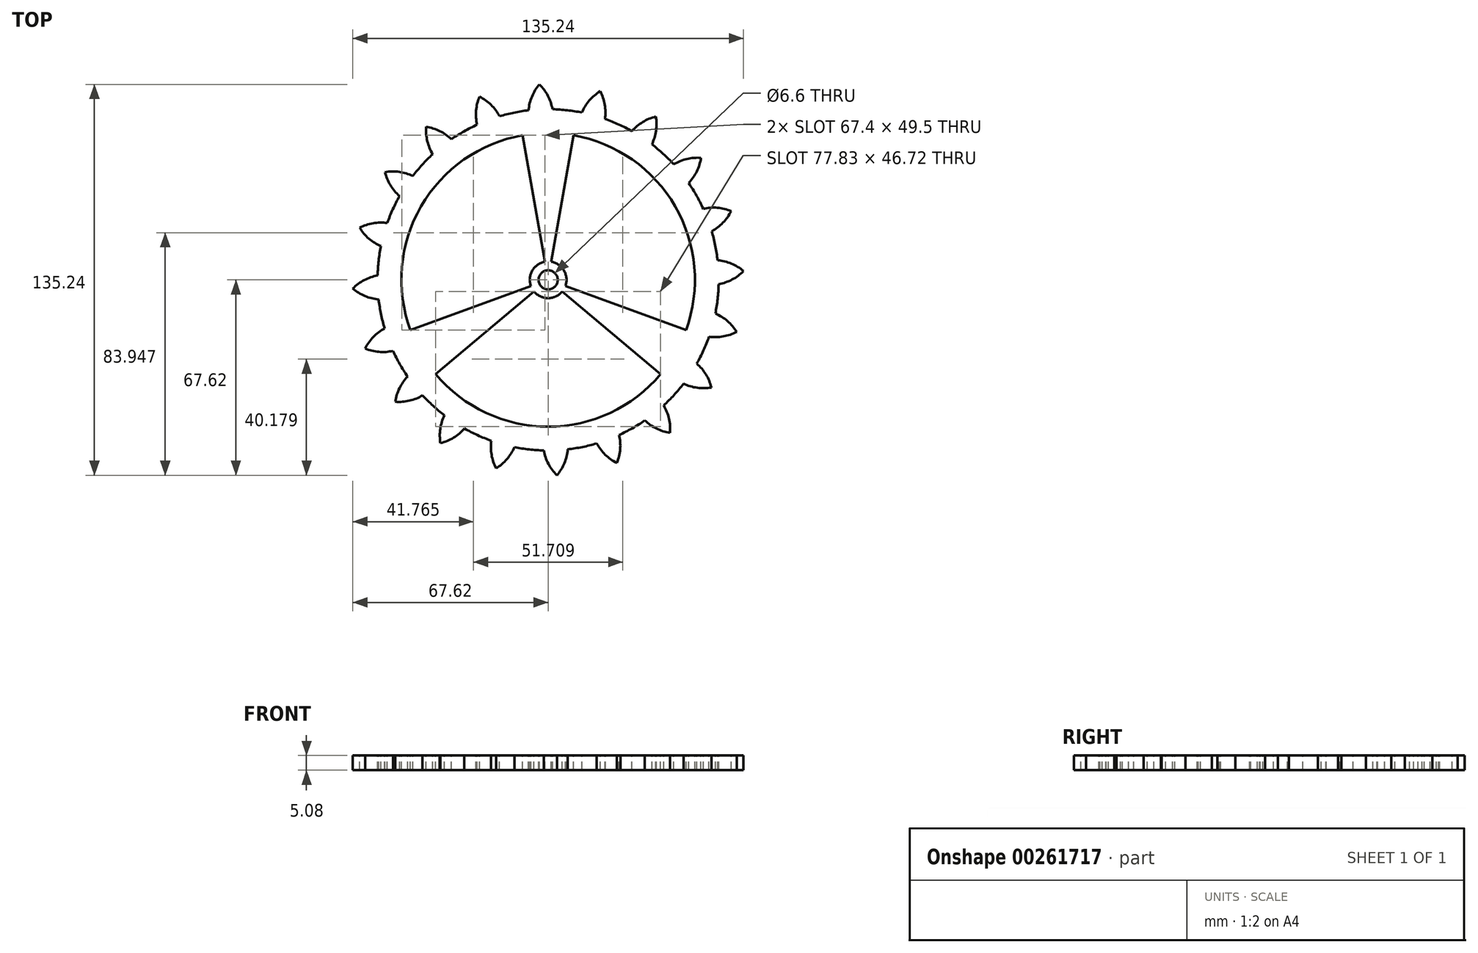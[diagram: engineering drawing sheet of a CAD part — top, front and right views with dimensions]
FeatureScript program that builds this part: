
annotation { "Feature Type Name" : "Feature", "Feature Type Description" : "" }
export const myFeature = defineFeature(function(context is Context, id is Id, definition is map)
    precondition{}
    {
        {
            var Q0;
            Q0=qCreatedBy(makeId("Top.planeOp"),FACE);
            var sketch = newSketch(context, id + "F0", { "sketchPlane" : qUnion([Q0])});
            skCircle(sketch, "E0", {"center": v(0, 0) * mm, "radius": 59.06 * mm});
            skSolve(sketch);
        }
        {
            var Q0;
            Q0=qSketchRegion(id+"F0",true);
            extrude(context, id + "F1", {"entities" : qUnion([Q0]), "depth" : 5.08 * mm});
        }
        {
            var Q0;
            Q0=makeQuery(id+"F1.opExtrude","CAP_FACE",FACE,{"disambiguationData":[OSD([sQuery(id+"F0.wireOp",EDGE,"E0")])],"isStart":false});
            var sketch = newSketch(context, id + "F2", { "sketchPlane" : qUnion([Q0])});
            skCircle(sketch, "E1", {"center": v(0, 0) * mm, "radius": 67.13 * mm, "construction": true});
            skCircle(sketch, "E2", {"center": v(0, 0) * mm, "radius": 63.5 * mm, "construction": true});
            skCircle(sketch, "E3", {"center": v(0, 0) * mm, "radius": 58.96 * mm, "construction": true});
            skLineSegment(sketch, "E4", {"start": v(0, 0) * mm, "end": v(0, 86.86) * mm, "construction": true});
            skLineSegment(sketch, "E5", {"start": v(0, 0) * mm, "end": v(-3.86, 85.95) * mm, "construction": true});
            skLineSegment(sketch, "E6", {"start": v(0, 63.5) * mm, "end": v(-65.71, 63.5) * mm, "construction": true});
            skLineSegment(sketch, "E7", {"start": v(0, 63.5) * mm, "end": v(-58.85, 37.3) * mm, "construction": true});
            skCircle(sketch, "E8", {"center": v(0, 63.5) * mm, "radius": 15.88 * mm, "construction": true});
            skCircle(sketch, "E9", {"center": v(0, 0) * mm, "radius": 58.01 * mm, "construction": true});
            skCircle(sketch, "E10", {"center": v(-14.13, 56.26) * mm, "radius": 15.88 * mm, "construction": true});
            skArc(sketch, "E11", {"start": v(1.52, 58.94) * mm, "mid": v(-0.07, 63.64) * mm, "end": v(-3.04, 67.62) * mm});
            skArc(sketch, "E12.MirrorCS", {"start": v(-6.8, 58.57) * mm, "mid": v(-5.63, 63.4) * mm, "end": v(-3.04, 67.62) * mm});
            skLineSegment(sketch, "E13", {"start": v(-6.8, 58.57) * mm, "end": v(1.52, 58.94) * mm});
            skPoint(sketch, "E14.orphan", {"position": v(-3.5, 67.04) * mm});
            skPoint(sketch, "E15.orphan", {"position": v(-2.51, 67.08) * mm});
            skSolve(sketch);
        }
        {
            var Q0;
            Q0=qSketchRegion(id+"F2",true);
            var Q1;
            Q1=makeQuery(id+"F1.opExtrude","CAP_FACE",FACE,{"disambiguationData":[OSD([sQuery(id+"F0.wireOp",EDGE,"E0")])],"isStart":true});
            extrude(context, id + "F3", {"entities" : qUnion([Q0]), "endBound" : BoundingType.UP_TO_SURFACE, "oppositeDirection" : true, "endBoundEntityFace" : qUnion([Q1]), "depth" : 25.4 * mm});
        }
        {
            var Q0;
            Q0=makeQuery(id+"F3.opExtrude","SWEPT_BODY",BODY,{"disambiguationData":[OSD([sQuery(id+"F2.wireOp",EDGE,"E11"),sQuery(id+"F2.wireOp",EDGE,"E12.MirrorCS"),sQuery(id+"F2.wireOp",EDGE,"E13")])]});
            var Q1;
            Q1=makeQuery(id+"F1.opExtrude","CAP_EDGE",EDGE,{"disambiguationData":[OSD([sQuery(id+"F0.wireOp",EDGE,"E0")])],"isStart":false});
            circularPattern(context, id + "F4", {"operationType" : NewBodyOperationType.ADD, "entities" : qUnion([Q0]), "axis" : qUnion([Q1]), "angle" : 360 * degree, "instanceCount" : 20, "equalSpace" : true});
        }
        {
            var Q0;
            {var subQ0=makeQuery(id+"F3.opExtrude","CAP_FACE",FACE,{"disambiguationData":[OSD([sQuery(id+"F2.wireOp",EDGE,"E11"),sQuery(id+"F2.wireOp",EDGE,"E12.MirrorCS"),sQuery(id+"F2.wireOp",EDGE,"E13")])],"isStart":true});Q0=makeQuery(id+"F4.boolean.opBoolean","MERGE",FACE,{"derivedFrom":[makeQuery(id+"F1.opExtrude","CAP_FACE",FACE,{"disambiguationData":[OSD([sQuery(id+"F0.wireOp",EDGE,"E0")])],"isStart":false}),subQ0,makeQuery(id+"F4.opPattern","COPY",FACE,{"derivedFrom":subQ0,"instanceName":"1"}),makeQuery(id+"F4.opPattern","COPY",FACE,{"derivedFrom":subQ0,"instanceName":"2"}),makeQuery(id+"F4.opPattern","COPY",FACE,{"derivedFrom":subQ0,"instanceName":"3"}),makeQuery(id+"F4.opPattern","COPY",FACE,{"derivedFrom":subQ0,"instanceName":"4"}),makeQuery(id+"F4.opPattern","COPY",FACE,{"derivedFrom":subQ0,"instanceName":"5"}),makeQuery(id+"F4.opPattern","COPY",FACE,{"derivedFrom":subQ0,"instanceName":"6"}),makeQuery(id+"F4.opPattern","COPY",FACE,{"derivedFrom":subQ0,"instanceName":"7"}),makeQuery(id+"F4.opPattern","COPY",FACE,{"derivedFrom":subQ0,"instanceName":"8"}),makeQuery(id+"F4.opPattern","COPY",FACE,{"derivedFrom":subQ0,"instanceName":"9"}),makeQuery(id+"F4.opPattern","COPY",FACE,{"derivedFrom":subQ0,"instanceName":"10"}),makeQuery(id+"F4.opPattern","COPY",FACE,{"derivedFrom":subQ0,"instanceName":"11"}),makeQuery(id+"F4.opPattern","COPY",FACE,{"derivedFrom":subQ0,"instanceName":"12"}),makeQuery(id+"F4.opPattern","COPY",FACE,{"derivedFrom":subQ0,"instanceName":"13"}),makeQuery(id+"F4.opPattern","COPY",FACE,{"derivedFrom":subQ0,"instanceName":"14"}),makeQuery(id+"F4.opPattern","COPY",FACE,{"derivedFrom":subQ0,"instanceName":"15"}),makeQuery(id+"F4.opPattern","COPY",FACE,{"derivedFrom":subQ0,"instanceName":"16"}),makeQuery(id+"F4.opPattern","COPY",FACE,{"derivedFrom":subQ0,"instanceName":"17"}),makeQuery(id+"F4.opPattern","COPY",FACE,{"derivedFrom":subQ0,"instanceName":"18"}),makeQuery(id+"F4.opPattern","COPY",FACE,{"derivedFrom":subQ0,"instanceName":"19"})]});}
            var sketch = newSketch(context, id + "F5", { "sketchPlane" : qUnion([Q0])});
            skCircle(sketch, "E16", {"center": v(0, 0) * mm, "radius": 50.8 * mm});
            skSolve(sketch);
        }
        {
            var Q0;
            Q0=qSketchRegion(id+"F5",true);
            extrude(context, id + "F6", {"entities" : qUnion([Q0]), "operationType" : NewBodyOperationType.REMOVE, "endBound" : BoundingType.THROUGH_ALL, "oppositeDirection" : true, "depth" : 25.4 * mm});
        }
        {
            var Q0;
            Q0=qSketchRegion(id+"F5",true);
            extrude(context, id + "F7", {"entities" : qUnion([Q0]), "operationType" : NewBodyOperationType.REMOVE, "endBound" : BoundingType.THROUGH_ALL, "oppositeDirection" : true, "depth" : 25.4 * mm});
        }
        {
            var Q0;
            {var subQ0=makeQuery(id+"F3.opExtrude","CAP_FACE",FACE,{"disambiguationData":[OSD([sQuery(id+"F2.wireOp",EDGE,"E11"),sQuery(id+"F2.wireOp",EDGE,"E12.MirrorCS"),sQuery(id+"F2.wireOp",EDGE,"E13")])],"isStart":true});Q0=makeQuery(id+"F4.boolean.opBoolean","MERGE",FACE,{"derivedFrom":[makeQuery(id+"F1.opExtrude","CAP_FACE",FACE,{"disambiguationData":[OSD([sQuery(id+"F0.wireOp",EDGE,"E0")])],"isStart":false}),subQ0,makeQuery(id+"F4.opPattern","COPY",FACE,{"derivedFrom":subQ0,"instanceName":"1"}),makeQuery(id+"F4.opPattern","COPY",FACE,{"derivedFrom":subQ0,"instanceName":"2"}),makeQuery(id+"F4.opPattern","COPY",FACE,{"derivedFrom":subQ0,"instanceName":"3"}),makeQuery(id+"F4.opPattern","COPY",FACE,{"derivedFrom":subQ0,"instanceName":"4"}),makeQuery(id+"F4.opPattern","COPY",FACE,{"derivedFrom":subQ0,"instanceName":"5"}),makeQuery(id+"F4.opPattern","COPY",FACE,{"derivedFrom":subQ0,"instanceName":"6"}),makeQuery(id+"F4.opPattern","COPY",FACE,{"derivedFrom":subQ0,"instanceName":"7"}),makeQuery(id+"F4.opPattern","COPY",FACE,{"derivedFrom":subQ0,"instanceName":"8"}),makeQuery(id+"F4.opPattern","COPY",FACE,{"derivedFrom":subQ0,"instanceName":"9"}),makeQuery(id+"F4.opPattern","COPY",FACE,{"derivedFrom":subQ0,"instanceName":"10"}),makeQuery(id+"F4.opPattern","COPY",FACE,{"derivedFrom":subQ0,"instanceName":"11"}),makeQuery(id+"F4.opPattern","COPY",FACE,{"derivedFrom":subQ0,"instanceName":"12"}),makeQuery(id+"F4.opPattern","COPY",FACE,{"derivedFrom":subQ0,"instanceName":"13"}),makeQuery(id+"F4.opPattern","COPY",FACE,{"derivedFrom":subQ0,"instanceName":"14"}),makeQuery(id+"F4.opPattern","COPY",FACE,{"derivedFrom":subQ0,"instanceName":"15"}),makeQuery(id+"F4.opPattern","COPY",FACE,{"derivedFrom":subQ0,"instanceName":"16"}),makeQuery(id+"F4.opPattern","COPY",FACE,{"derivedFrom":subQ0,"instanceName":"17"}),makeQuery(id+"F4.opPattern","COPY",FACE,{"derivedFrom":subQ0,"instanceName":"18"}),makeQuery(id+"F4.opPattern","COPY",FACE,{"derivedFrom":subQ0,"instanceName":"19"})]});}
            var sketch = newSketch(context, id + "F8", { "sketchPlane" : qUnion([Q0])});
            skArc(sketch, "E17", {"start": v(-1.1, 6.25) * mm, "mid": v(0, -6.35) * mm, "end": v(1.1, 6.25) * mm});
            skLineSegment(sketch, "E18", {"start": v(-1.1, 6.25) * mm, "end": v(-8.82, 50.03) * mm});
            skArc(sketch, "E19", {"start": v(8.82, 50.03) * mm, "mid": v(0, 50.8) * mm, "end": v(-8.82, 50.03) * mm});
            skLineSegment(sketch, "E20", {"start": v(8.82, 50.03) * mm, "end": v(1.1, 6.25) * mm});
            skSolve(sketch);
        }
        {
            var Q0;
            Q0=qSketchRegion(id+"F8",true);
            var Q1;
            {var subQ0=makeQuery(id+"F3.opExtrude","CAP_FACE",FACE,{"disambiguationData":[OSD([sQuery(id+"F2.wireOp",EDGE,"E11"),sQuery(id+"F2.wireOp",EDGE,"E12.MirrorCS"),sQuery(id+"F2.wireOp",EDGE,"E13")])],"isStart":false});Q1=makeQuery(id+"F4.boolean.opBoolean","MERGE",FACE,{"derivedFrom":[makeQuery(id+"F1.opExtrude","CAP_FACE",FACE,{"disambiguationData":[OSD([sQuery(id+"F0.wireOp",EDGE,"E0")])],"isStart":true}),subQ0,makeQuery(id+"F4.opPattern","COPY",FACE,{"derivedFrom":subQ0,"instanceName":"1"}),makeQuery(id+"F4.opPattern","COPY",FACE,{"derivedFrom":subQ0,"instanceName":"2"}),makeQuery(id+"F4.opPattern","COPY",FACE,{"derivedFrom":subQ0,"instanceName":"3"}),makeQuery(id+"F4.opPattern","COPY",FACE,{"derivedFrom":subQ0,"instanceName":"4"}),makeQuery(id+"F4.opPattern","COPY",FACE,{"derivedFrom":subQ0,"instanceName":"5"}),makeQuery(id+"F4.opPattern","COPY",FACE,{"derivedFrom":subQ0,"instanceName":"6"}),makeQuery(id+"F4.opPattern","COPY",FACE,{"derivedFrom":subQ0,"instanceName":"7"}),makeQuery(id+"F4.opPattern","COPY",FACE,{"derivedFrom":subQ0,"instanceName":"8"}),makeQuery(id+"F4.opPattern","COPY",FACE,{"derivedFrom":subQ0,"instanceName":"9"}),makeQuery(id+"F4.opPattern","COPY",FACE,{"derivedFrom":subQ0,"instanceName":"10"}),makeQuery(id+"F4.opPattern","COPY",FACE,{"derivedFrom":subQ0,"instanceName":"11"}),makeQuery(id+"F4.opPattern","COPY",FACE,{"derivedFrom":subQ0,"instanceName":"12"}),makeQuery(id+"F4.opPattern","COPY",FACE,{"derivedFrom":subQ0,"instanceName":"13"}),makeQuery(id+"F4.opPattern","COPY",FACE,{"derivedFrom":subQ0,"instanceName":"14"}),makeQuery(id+"F4.opPattern","COPY",FACE,{"derivedFrom":subQ0,"instanceName":"15"}),makeQuery(id+"F4.opPattern","COPY",FACE,{"derivedFrom":subQ0,"instanceName":"16"}),makeQuery(id+"F4.opPattern","COPY",FACE,{"derivedFrom":subQ0,"instanceName":"17"}),makeQuery(id+"F4.opPattern","COPY",FACE,{"derivedFrom":subQ0,"instanceName":"18"}),makeQuery(id+"F4.opPattern","COPY",FACE,{"derivedFrom":subQ0,"instanceName":"19"})]});}
            extrude(context, id + "F9", {"entities" : qUnion([Q0]), "endBound" : BoundingType.UP_TO_SURFACE, "oppositeDirection" : true, "endBoundEntityFace" : qUnion([Q1]), "depth" : 25.4 * mm});
        }
        {
            var Q0;
            Q0=makeQuery(id+"F9.opExtrude","SWEPT_BODY",BODY,{"disambiguationData":[OSD([sQuery(id+"F8.wireOp",EDGE,"E17"),sQuery(id+"F8.wireOp",EDGE,"E18"),sQuery(id+"F8.wireOp",EDGE,"E19"),sQuery(id+"F8.wireOp",EDGE,"E20")])]});
            var Q1;
            Q1=makeQuery(id+"F9.opExtrude","SWEPT_FACE",FACE,{"disambiguationData":[OSD([sQuery(id+"F8.wireOp",EDGE,"E17")])]});
            circularPattern(context, id + "F10", {"operationType" : NewBodyOperationType.ADD, "entities" : qUnion([Q0]), "axis" : qUnion([Q1]), "angle" : 360 * degree, "instanceCount" : 3, "equalSpace" : true});
        }
        {
            var Q0;
            {var subQ0=makeQuery(id+"F9.opExtrude","CAP_FACE",FACE,{"disambiguationData":[OSD([sQuery(id+"F8.wireOp",EDGE,"E17"),sQuery(id+"F8.wireOp",EDGE,"E18"),sQuery(id+"F8.wireOp",EDGE,"E19"),sQuery(id+"F8.wireOp",EDGE,"E20")])],"isStart":true});var subQ1=makeQuery(id+"F3.opExtrude","CAP_FACE",FACE,{"disambiguationData":[OSD([sQuery(id+"F2.wireOp",EDGE,"E11"),sQuery(id+"F2.wireOp",EDGE,"E12.MirrorCS"),sQuery(id+"F2.wireOp",EDGE,"E13")])],"isStart":true});Q0=makeQuery(id+"F10.boolean.opBoolean","MERGE",FACE,{"derivedFrom":[makeQuery(id+"F4.boolean.opBoolean","MERGE",FACE,{"derivedFrom":[makeQuery(id+"F1.opExtrude","CAP_FACE",FACE,{"disambiguationData":[OSD([sQuery(id+"F0.wireOp",EDGE,"E0")])],"isStart":false}),subQ1,makeQuery(id+"F4.opPattern","COPY",FACE,{"derivedFrom":subQ1,"instanceName":"1"}),makeQuery(id+"F4.opPattern","COPY",FACE,{"derivedFrom":subQ1,"instanceName":"2"}),makeQuery(id+"F4.opPattern","COPY",FACE,{"derivedFrom":subQ1,"instanceName":"3"}),makeQuery(id+"F4.opPattern","COPY",FACE,{"derivedFrom":subQ1,"instanceName":"4"}),makeQuery(id+"F4.opPattern","COPY",FACE,{"derivedFrom":subQ1,"instanceName":"5"}),makeQuery(id+"F4.opPattern","COPY",FACE,{"derivedFrom":subQ1,"instanceName":"6"}),makeQuery(id+"F4.opPattern","COPY",FACE,{"derivedFrom":subQ1,"instanceName":"7"}),makeQuery(id+"F4.opPattern","COPY",FACE,{"derivedFrom":subQ1,"instanceName":"8"}),makeQuery(id+"F4.opPattern","COPY",FACE,{"derivedFrom":subQ1,"instanceName":"9"}),makeQuery(id+"F4.opPattern","COPY",FACE,{"derivedFrom":subQ1,"instanceName":"10"}),makeQuery(id+"F4.opPattern","COPY",FACE,{"derivedFrom":subQ1,"instanceName":"11"}),makeQuery(id+"F4.opPattern","COPY",FACE,{"derivedFrom":subQ1,"instanceName":"12"}),makeQuery(id+"F4.opPattern","COPY",FACE,{"derivedFrom":subQ1,"instanceName":"13"}),makeQuery(id+"F4.opPattern","COPY",FACE,{"derivedFrom":subQ1,"instanceName":"14"}),makeQuery(id+"F4.opPattern","COPY",FACE,{"derivedFrom":subQ1,"instanceName":"15"}),makeQuery(id+"F4.opPattern","COPY",FACE,{"derivedFrom":subQ1,"instanceName":"16"}),makeQuery(id+"F4.opPattern","COPY",FACE,{"derivedFrom":subQ1,"instanceName":"17"}),makeQuery(id+"F4.opPattern","COPY",FACE,{"derivedFrom":subQ1,"instanceName":"18"}),makeQuery(id+"F4.opPattern","COPY",FACE,{"derivedFrom":subQ1,"instanceName":"19"})]}),subQ0,makeQuery(id+"F10.opPattern","COPY",FACE,{"derivedFrom":subQ0,"instanceName":"1"}),makeQuery(id+"F10.opPattern","COPY",FACE,{"derivedFrom":subQ0,"instanceName":"2"})]});}
            var sketch = newSketch(context, id + "F11", { "sketchPlane" : qUnion([Q0])});
            skCircle(sketch, "E21", {"center": v(0, 0) * mm, "radius": 3.3 * mm});
            skSolve(sketch);
        }
        {
            var Q0;
            Q0=qSketchRegion(id+"F11",true);
            extrude(context, id + "F12", {"entities" : qUnion([Q0]), "operationType" : NewBodyOperationType.REMOVE, "endBound" : BoundingType.THROUGH_ALL, "oppositeDirection" : true, "depth" : 25.4 * mm});
        }
    });
